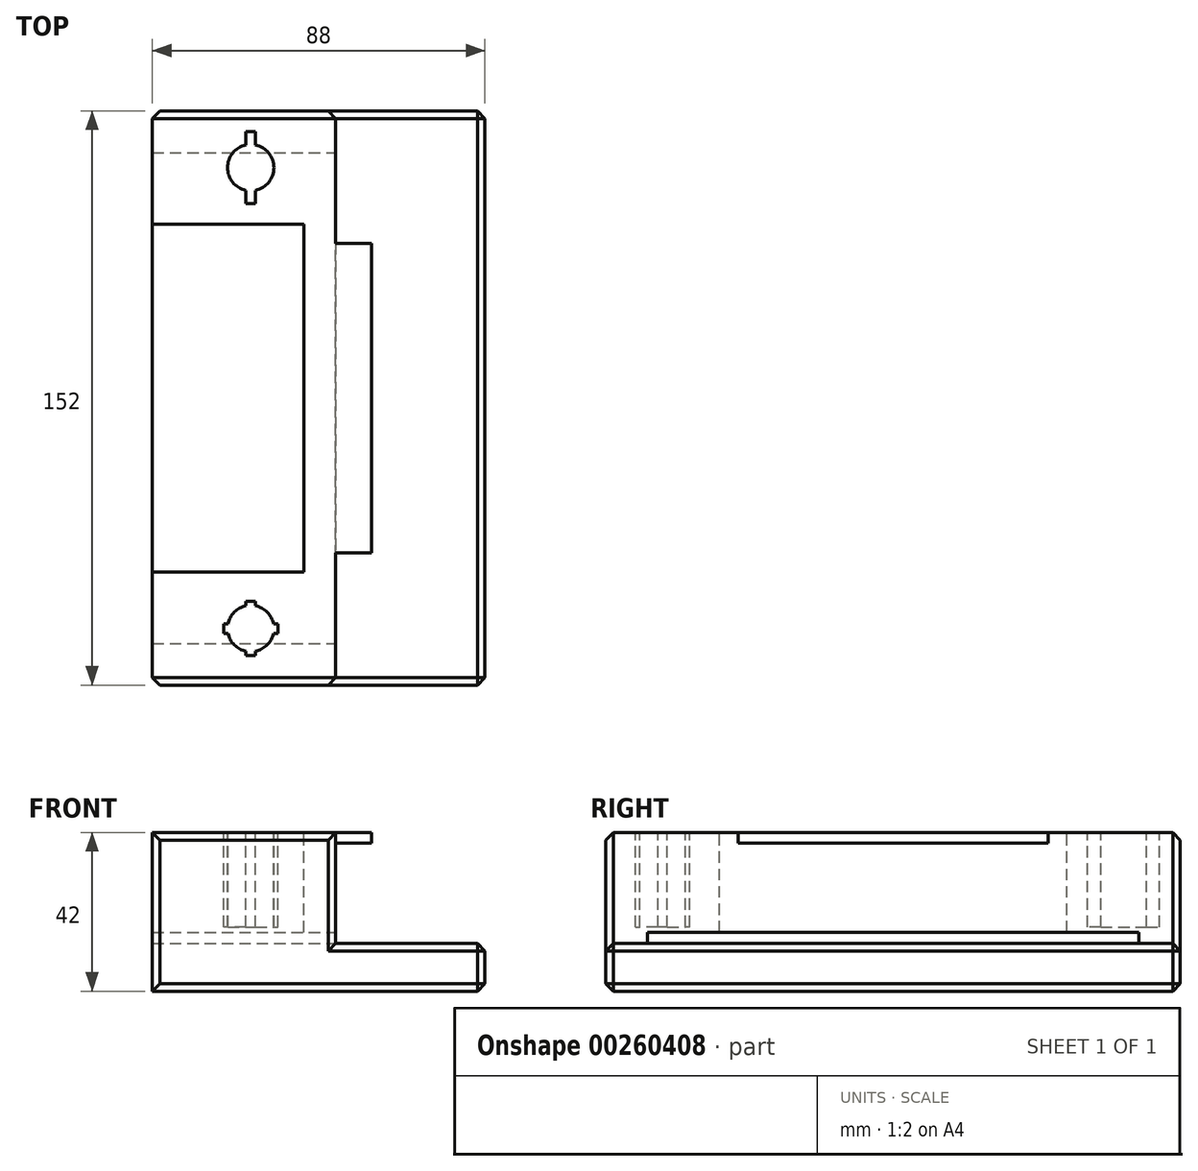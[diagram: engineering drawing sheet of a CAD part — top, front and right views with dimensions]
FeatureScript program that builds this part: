
annotation { "Feature Type Name" : "Feature", "Feature Type Description" : "" }
export const myFeature = defineFeature(function(context is Context, id is Id, definition is map)
    precondition{}
    {
        {
            var Q0;
            Q0=qCreatedBy(makeId("Top.planeOp"),FACE);
            var sketch = newSketch(context, id + "F0", { "sketchPlane" : qUnion([Q0])});
            skLineSegment(sketch, "E0.bottom", {"start": v(-48.09, -38.91) * mm, "end": v(9.91, -38.91) * mm});
            skLineSegment(sketch, "E0.top", {"start": v(-48.09, 113.09) * mm, "end": v(9.91, 113.09) * mm});
            skLineSegment(sketch, "E0.left", {"start": v(-48.09, -38.91) * mm, "end": v(-48.09, 113.09) * mm});
            skLineSegment(sketch, "E0.right", {"start": v(9.91, -38.91) * mm, "end": v(9.91, 113.09) * mm});
            skSolve(sketch);
        }
        {
            var Q0;
            Q0=makeQuery(id+"F0.imprint","IMPRINT",FACE,{"disambiguationData":[TD([[makeQuery(id+"F0.imprint","IMPRINT",EDGE,{"derivedFrom":sQuery(id+"F0.wireOp",EDGE,"E0.bottom")}),1.0]])]});
            extrude(context, id + "F1", {"entities" : qUnion([Q0]), "depth" : 42 * mm});
        }
        {
            var Q0;
            Q0=makeQuery(id+"F1.opExtrude","CAP_FACE",FACE,{"disambiguationData":[OSD([sQuery(id+"F0.wireOp",EDGE,"E0.bottom"),sQuery(id+"F0.wireOp",EDGE,"E0.top"),sQuery(id+"F0.wireOp",EDGE,"E0.left"),sQuery(id+"F0.wireOp",EDGE,"E0.right")])],"isStart":false});
            var sketch = newSketch(context, id + "F2", { "sketchPlane" : qUnion([Q0])});
            skPoint(sketch, "E1", {"position": v(9.91, 37.09) * mm});
            skPoint(sketch, "E2", {"position": v(-22.09, -23.91) * mm});
            skPoint(sketch, "E3", {"position": v(-22.09, 98.09) * mm});
            skArc(sketch, "E4", {"start": v(-20.84, -29.93) * mm, "mid": v(-17.74, -28.26) * mm, "end": v(-16.07, -25.16) * mm});
            skArc(sketch, "E5", {"start": v(-20.84, 92.07) * mm, "mid": v(-15.94, 98.09) * mm, "end": v(-20.84, 104.1) * mm});
            skLineSegment(sketch, "E6", {"start": v(-23.34, 92.07) * mm, "end": v(-23.34, 88.59) * mm});
            skLineSegment(sketch, "E7", {"start": v(-20.84, 92.07) * mm, "end": v(-20.84, 88.59) * mm});
            skLineSegment(sketch, "E8", {"start": v(-23.34, 104.1) * mm, "end": v(-23.34, 107.59) * mm});
            skLineSegment(sketch, "E9", {"start": v(-20.84, 104.1) * mm, "end": v(-20.84, 107.59) * mm});
            skLineSegment(sketch, "E10", {"start": v(-23.34, 107.59) * mm, "end": v(-20.84, 107.59) * mm});
            skLineSegment(sketch, "E11", {"start": v(-23.34, 88.59) * mm, "end": v(-20.84, 88.59) * mm});
            skPoint(sketch, "E12.orphan", {"position": v(-0.09, 88.59) * mm});
            skPoint(sketch, "E13.orphan", {"position": v(-20.84, 98.09) * mm});
            skPoint(sketch, "E14.orphan", {"position": v(-23.34, 98.09) * mm});
            skArc(sketch, "E15.trimOffspring", {"start": v(-23.34, 104.1) * mm, "mid": v(-28.24, 98.09) * mm, "end": v(-23.34, 92.07) * mm});
            skLineSegment(sketch, "E16", {"start": v(-23.34, -29.93) * mm, "end": v(-23.34, -31.06) * mm, "construction": true});
            skLineSegment(sketch, "E17", {"start": v(-23.34, -31.06) * mm, "end": v(-23.34, -29.93) * mm});
            skLineSegment(sketch, "E18", {"start": v(-20.84, -17.9) * mm, "end": v(-20.84, -16.76) * mm, "construction": true});
            skLineSegment(sketch, "E19", {"start": v(-20.84, -16.76) * mm, "end": v(-20.84, -17.9) * mm});
            skLineSegment(sketch, "E20", {"start": v(-20.84, -16.76) * mm, "end": v(-0.09, -16.76) * mm});
            skLineSegment(sketch, "E21", {"start": v(-20.84, -31.06) * mm, "end": v(-0.09, -31.06) * mm});
            skLineSegment(sketch, "E22", {"start": v(-0.09, -31.06) * mm, "end": v(-23.34, -31.06) * mm});
            skArc(sketch, "E23.trimOffspring", {"start": v(-23.34, -17.9) * mm, "mid": v(-26.44, -19.56) * mm, "end": v(-28.11, -22.66) * mm});
            skLineSegment(sketch, "E24.trimOffspring", {"start": v(-23.34, -17.9) * mm, "end": v(-23.34, -16.76) * mm});
            skLineSegment(sketch, "E25.trimOffspring", {"start": v(-20.84, -29.93) * mm, "end": v(-20.84, -31.06) * mm});
            skLineSegment(sketch, "E26", {"start": v(-23.34, -16.76) * mm, "end": v(-0.09, -16.76) * mm});
            skLineSegment(sketch, "E27", {"start": v(-28.11, -25.16) * mm, "end": v(-29.24, -25.16) * mm});
            skLineSegment(sketch, "E28", {"start": v(-28.11, -22.66) * mm, "end": v(-29.24, -22.66) * mm});
            skLineSegment(sketch, "E29", {"start": v(-16.07, -22.66) * mm, "end": v(-14.94, -22.66) * mm});
            skLineSegment(sketch, "E30", {"start": v(-16.07, -25.16) * mm, "end": v(-14.94, -25.16) * mm});
            skLineSegment(sketch, "E31", {"start": v(-29.24, -22.66) * mm, "end": v(-29.24, -25.16) * mm});
            skLineSegment(sketch, "E32", {"start": v(-14.94, -22.66) * mm, "end": v(-14.94, -25.16) * mm});
            skArc(sketch, "E33.trimOffspring", {"start": v(-28.11, -25.16) * mm, "mid": v(-26.44, -28.26) * mm, "end": v(-23.34, -29.93) * mm});
            skArc(sketch, "E34.trimOffspring", {"start": v(-16.07, -22.66) * mm, "mid": v(-17.74, -19.56) * mm, "end": v(-20.84, -17.9) * mm});
            skPoint(sketch, "E35.orphan", {"position": v(-22.09, -25.16) * mm});
            skPoint(sketch, "E36.orphan", {"position": v(-22.09, -22.66) * mm});
            skSolve(sketch);
        }
        {
            var Q0;
            Q0=makeQuery(id+"F2.imprint","IMPRINT",FACE,{"disambiguationData":[TD([[makeQuery(id+"F2.imprint","IMPRINT",EDGE,{"derivedFrom":sQuery(id+"F2.wireOp",EDGE,"E5")}),1.0]])]});
            extrude(context, id + "F3", {"entities" : qUnion([Q0]), "operationType" : NewBodyOperationType.REMOVE, "oppositeDirection" : true, "depth" : 25 * mm});
        }
        {
            var Q0;
            Q0=makeQuery(id+"F2.imprint","IMPRINT",FACE,{"disambiguationData":[TD([[makeQuery(id+"F2.imprint","IMPRINT",EDGE,{"derivedFrom":sQuery(id+"F2.wireOp",EDGE,"E4")}),1.0]])]});
            extrude(context, id + "F4", {"entities" : qUnion([Q0]), "operationType" : NewBodyOperationType.REMOVE, "oppositeDirection" : true, "depth" : 25 * mm});
        }
        {
            var Q0;
            Q0=makeQuery(id+"F1.opExtrude","SWEPT_FACE",FACE,{"disambiguationData":[OSD([sQuery(id+"F0.wireOp",EDGE,"E0.right")])]});
            var sketch = newSketch(context, id + "F5", { "sketchPlane" : qUnion([Q0])});
            skLineSegment(sketch, "E37.bottom", {"start": v(-27.91, 15.6) * mm, "end": v(102.09, 15.6) * mm});
            skLineSegment(sketch, "E37.top", {"start": v(-27.91, 12.6) * mm, "end": v(102.09, 12.6) * mm});
            skLineSegment(sketch, "E37.left", {"start": v(-27.91, 15.6) * mm, "end": v(-27.91, 12.6) * mm});
            skLineSegment(sketch, "E37.right", {"start": v(102.09, 15.6) * mm, "end": v(102.09, 12.6) * mm});
            skLineSegment(sketch, "E38.bottom", {"start": v(-38.91, 12.6) * mm, "end": v(113.09, 12.6) * mm});
            skLineSegment(sketch, "E38.top", {"start": v(-38.91, 0) * mm, "end": v(113.09, 0) * mm});
            skLineSegment(sketch, "E38.left", {"start": v(-38.91, 12.6) * mm, "end": v(-38.91, 0) * mm});
            skLineSegment(sketch, "E38.right", {"start": v(113.09, 12.6) * mm, "end": v(113.09, 0) * mm});
            skSolve(sketch);
        }
        {
            var Q0;
            Q0=makeQuery(id+"F5.imprint","IMPRINT",FACE,{"disambiguationData":[TD([[makeQuery(id+"F5.imprint","IMPRINT",EDGE,{"derivedFrom":sQuery(id+"F5.wireOp",EDGE,"E37.bottom")}),-1.0]])]});
            extrude(context, id + "F6", {"entities" : qUnion([Q0]), "operationType" : NewBodyOperationType.REMOVE, "endBound" : BoundingType.UP_TO_NEXT, "oppositeDirection" : true, "depth" : 25 * mm});
        }
        {
            var Q0;
            Q0=makeQuery(id+"F5.imprint","IMPRINT",FACE,{"disambiguationData":[TD([[makeQuery(id+"F5.imprint","IMPRINT",EDGE,{"derivedFrom":sQuery(id+"F5.wireOp",EDGE,"E38.top")}),1.0]])]});
            extrude(context, id + "F7", {"entities" : qUnion([Q0]), "operationType" : NewBodyOperationType.ADD, "depth" : 30 * mm});
        }
        {
            var Q0;
            Q0=makeQuery(id+"F1.opExtrude","CAP_FACE",FACE,{"disambiguationData":[OSD([sQuery(id+"F0.wireOp",EDGE,"E0.bottom"),sQuery(id+"F0.wireOp",EDGE,"E0.top"),sQuery(id+"F0.wireOp",EDGE,"E0.left"),sQuery(id+"F0.wireOp",EDGE,"E0.right")])],"isStart":false});
            var sketch = newSketch(context, id + "F8", { "sketchPlane" : qUnion([Q0])});
            skLineSegment(sketch, "E39.bottom", {"start": v(9.91, -38.91) * mm, "end": v(0.41, -38.91) * mm});
            skLineSegment(sketch, "E39.top", {"start": v(9.91, -3.91) * mm, "end": v(0.41, -3.91) * mm});
            skLineSegment(sketch, "E39.left", {"start": v(9.91, -38.91) * mm, "end": v(9.91, -3.91) * mm});
            skLineSegment(sketch, "E39.right", {"start": v(0.41, -38.91) * mm, "end": v(0.41, -3.91) * mm});
            skLineSegment(sketch, "E40.bottom", {"start": v(9.91, 113.09) * mm, "end": v(0.41, 113.09) * mm});
            skLineSegment(sketch, "E40.top", {"start": v(9.91, 78.09) * mm, "end": v(0.41, 78.09) * mm});
            skLineSegment(sketch, "E40.left", {"start": v(9.91, 113.09) * mm, "end": v(9.91, 78.09) * mm});
            skLineSegment(sketch, "E40.right", {"start": v(0.41, 113.09) * mm, "end": v(0.41, 78.09) * mm});
            skSolve(sketch);
        }
        {
            var Q0;
            Q0=makeQuery(id+"F8.imprint","IMPRINT",FACE,{"disambiguationData":[TD([[makeQuery(id+"F8.imprint","IMPRINT",EDGE,{"derivedFrom":sQuery(id+"F8.wireOp",EDGE,"E39.bottom")}),1.0]])]});
            var Q1;
            Q1=makeQuery(id+"F8.imprint","IMPRINT",FACE,{"disambiguationData":[TD([[makeQuery(id+"F8.imprint","IMPRINT",EDGE,{"derivedFrom":sQuery(id+"F8.wireOp",EDGE,"E40.bottom")}),-1.0]])]});
            var Q2;
            {var subQ0=sQuery(id+"F5.wireOp",EDGE,"E38.bottom");Q2=makeQuery(id+"F7.boolean.opBoolean","MERGE",FACE,{"derivedFrom":[makeQuery(id+"F6.boolean.opBoolean","COPY",FACE,{"derivedFrom":makeQuery(id+"F6.opExtrude","SWEPT_FACE",FACE,{"disambiguationData":[OSD([subQ0])]})}),makeQuery(id+"F7.opExtrude","SWEPT_FACE",FACE,{"disambiguationData":[OSD([subQ0])]})]});}
            extrude(context, id + "F9", {"entities" : qUnion([Q0, Q1]), "operationType" : NewBodyOperationType.REMOVE, "endBound" : BoundingType.UP_TO_SURFACE, "oppositeDirection" : true, "endBoundEntityFace" : qUnion([Q2]), "depth" : 25 * mm});
        }
        {
            var Q0;
            Q0=makeQuery(id+"F9.boolean.opBoolean","COPY",FACE,{"derivedFrom":makeQuery(id+"F9.opExtrude","SWEPT_FACE",FACE,{"disambiguationData":[OSD([sQuery(id+"F8.wireOp",EDGE,"E39.top")])]})});
            var sketch = newSketch(context, id + "F10", { "sketchPlane" : qUnion([Q0])});
            skLineSegment(sketch, "E41", {"start": v(0.41, 39.2) * mm, "end": v(9.91, 39.2) * mm});
            skSolve(sketch);
        }
        {
            var Q0;
            {var subQ0=sQuery(id+"F10.wireOp",EDGE,"E41");Q0=makeQuery(id+"F10.imprint","IMPRINT",FACE,{"disambiguationData":[TD([[makeQuery(id+"F10.imprint","IMPRINT",EDGE,{"derivedFrom":subQ0}),-1.0]])]});}
            var Q1;
            Q1=makeQuery(id+"F9.boolean.opBoolean","COPY",FACE,{"derivedFrom":makeQuery(id+"F9.opExtrude","SWEPT_FACE",FACE,{"disambiguationData":[OSD([sQuery(id+"F8.wireOp",EDGE,"E40.top")])]})});
            extrude(context, id + "F11", {"entities" : qUnion([Q0]), "operationType" : NewBodyOperationType.REMOVE, "endBound" : BoundingType.UP_TO_SURFACE, "oppositeDirection" : true, "endBoundEntityFace" : qUnion([Q1]), "depth" : 25 * mm});
        }
        {
            var Q0;
            Q0=makeQuery(id+"F7.boolean.opBoolean","MERGE",FACE,{"derivedFrom":[makeQuery(id+"F1.opExtrude","SWEPT_FACE",FACE,{"disambiguationData":[OSD([sQuery(id+"F0.wireOp",EDGE,"E0.bottom")])]}),makeQuery(id+"F7.opExtrude","SWEPT_FACE",FACE,{"disambiguationData":[OSD([sQuery(id+"F5.wireOp",EDGE,"E38.left")])]})]});
            var Q1;
            Q1=makeQuery(id+"F7.boolean.opBoolean","MERGE",FACE,{"derivedFrom":[makeQuery(id+"F1.opExtrude","SWEPT_FACE",FACE,{"disambiguationData":[OSD([sQuery(id+"F0.wireOp",EDGE,"E0.top")])]}),makeQuery(id+"F7.opExtrude","SWEPT_FACE",FACE,{"disambiguationData":[OSD([sQuery(id+"F5.wireOp",EDGE,"E38.right")])]})]});
            var Q2;
            Q2=makeQuery(id+"F7.opExtrude","CAP_FACE",FACE,{"disambiguationData":[OSD([sQuery(id+"F5.wireOp",EDGE,"E38.bottom"),sQuery(id+"F5.wireOp",EDGE,"E38.top"),sQuery(id+"F5.wireOp",EDGE,"E38.left"),sQuery(id+"F5.wireOp",EDGE,"E38.right")])],"isStart":false});
            chamfer(context, id + "F12", {"entities" : qUnion([Q0, Q1, Q2]), "width" : 2 * mm, "tangentPropagation" : true});
        }
        {
            var Q0;
            Q0=makeQuery(id+"F1.opExtrude","CAP_FACE",FACE,{"disambiguationData":[OSD([sQuery(id+"F0.wireOp",EDGE,"E0.bottom"),sQuery(id+"F0.wireOp",EDGE,"E0.top"),sQuery(id+"F0.wireOp",EDGE,"E0.left"),sQuery(id+"F0.wireOp",EDGE,"E0.right")])],"isStart":false});
            var sketch = newSketch(context, id + "F13", { "sketchPlane" : qUnion([Q0])});
            skLineSegment(sketch, "E42.bottom", {"start": v(-48.09, 83.09) * mm, "end": v(-8.09, 83.09) * mm});
            skLineSegment(sketch, "E42.top", {"start": v(-48.09, -8.91) * mm, "end": v(-8.09, -8.91) * mm});
            skLineSegment(sketch, "E42.left", {"start": v(-48.09, 83.09) * mm, "end": v(-48.09, -8.91) * mm});
            skLineSegment(sketch, "E42.right", {"start": v(-8.09, 83.09) * mm, "end": v(-8.09, -8.91) * mm});
            skSolve(sketch);
        }
        {
            var Q0;
            Q0=makeQuery(id+"F13.imprint","IMPRINT",FACE,{"disambiguationData":[TD([[makeQuery(id+"F13.imprint","IMPRINT",EDGE,{"derivedFrom":sQuery(id+"F13.wireOp",EDGE,"E42.bottom")}),-1.0]])]});
            extrude(context, id + "F14", {"entities" : qUnion([Q0]), "operationType" : NewBodyOperationType.REMOVE, "endBound" : BoundingType.UP_TO_NEXT, "oppositeDirection" : true, "depth" : 25 * mm});
        }
    });
